# Revit family: MTXTYP009
name_source: partatom
category: Furniture
units: mm (PartAtom-declared; Revit-internal decimal feet)

## family parameters
Always vertical = Yes
Cut with Voids When Loaded = No
OmniClass Number = 23.40.20.00
OmniClass Title = General Furniture and Specialties
Render Appearance Source = Family Geometry
Room Calculation Point = No
Shared = No
Work Plane-Based = No

## types (1)
- MTXTYP009
    Cost = 61967 $
    Default Elevation = 0 mm  [stored 0 ft]
    Description = 2 x Combo B/F Ped Left-Bookcase Right on Feet-18Dx21Hx48W, 2 x Combo B/F Ped Right/Bookcase Left on Feet-18Dx21Hx48W, 2 x Matrix Black Duplex Outlet - Line 1, 2 x Matrix Black Duplex Outlet - Line 2, 2 x Matrix Black Duplex Outlet - Line 3, 2 x Matrix Black Duplex Outlet - Line 4 - Dedicated, 2 x 18 in. Electrical Jumper  (Panel To Panel), 1 x 21 in. Electrical Jumper  (Extended Panel To Panel), 4 x Single Powerway Assembly - 36W - 8 wire, 4 circuit, 1 x LH Receptacle Mounted Base Infeed - 72L - 8 Wire, 4 Circuit, 8 x Quad Electrical Tile - 8H X 36W, 8 x Tackable Acoustical Tile - 32H x 36W, 24 x Tackable Acoustical Tile - 40H x 36W, 2 x 3-Way  90 Degree Connector - Linear Trim - 42H, 8 x MATRIX LINEAR Double Frame Recessed Glass Kit 36" & 36", 6 x Frame End Cap - Linear Trim - 42H, 16 x Panel Frame - Linear Trim - 42H x 36W, 8 x MATRIX RECESSED FRAMELESS GLASS 12"H X 72"W V2, 1 x 4-Way 90 Degree Connector - Linear Trim - 42H, 4 x TBL, REC, 2MM, 30DX72WX29H, HAL, E SERIES GLD 2 STAGE
    Exported From CET Designer = Yes
    Manufacturer = AIS
    Model = C-BFCBCL214818
    Show MTXTYP009 = Yes
    VisibilityIndex = 0

note: [stored X ft] marks values corroborated as IEEE doubles in the binary element streams (Revit-internal decimal feet)

## geometry (parser evidence)
native form markers: Sweep x3
no freeform markers — native parametric forms only
